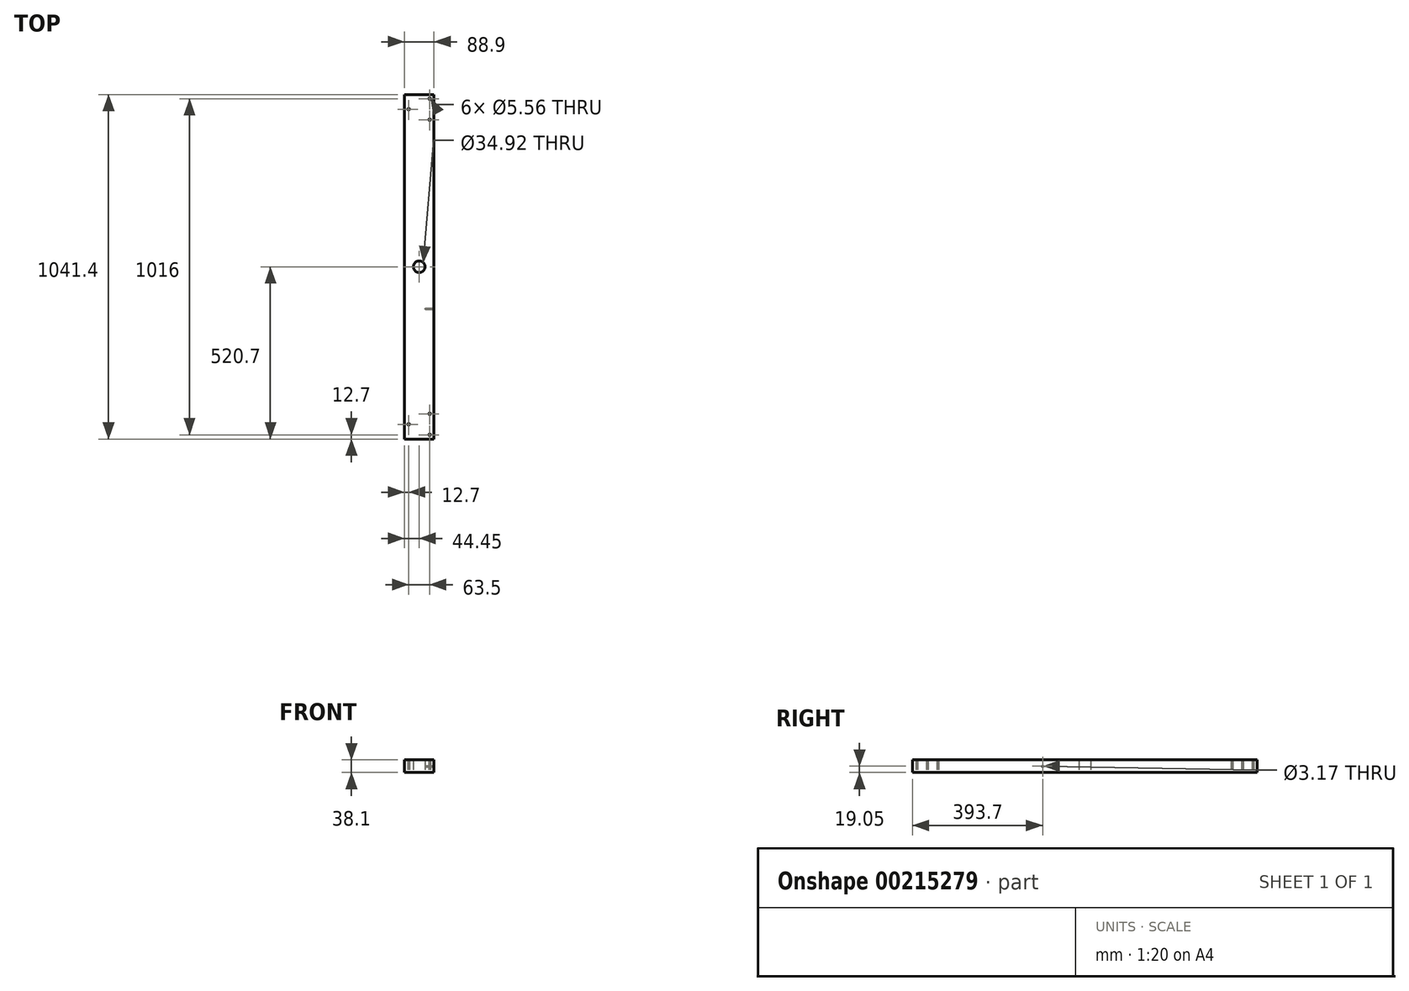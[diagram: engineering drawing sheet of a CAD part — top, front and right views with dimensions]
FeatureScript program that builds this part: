
annotation { "Feature Type Name" : "Feature", "Feature Type Description" : "" }
export const myFeature = defineFeature(function(context is Context, id is Id, definition is map)
    precondition{}
    {
        {
            var Q0;
            Q0=qCreatedBy(makeId("Top.planeOp"),FACE);
            var sketch = newSketch(context, id + "F0", { "sketchPlane" : qUnion([Q0])});
            skLineSegment(sketch, "E0.bottom", {"start": v(-44.45, 520.7) * mm, "end": v(44.45, 520.7) * mm});
            skLineSegment(sketch, "E0.top", {"start": v(-44.45, -520.7) * mm, "end": v(44.45, -520.7) * mm});
            skLineSegment(sketch, "E0.left", {"start": v(-44.45, 520.7) * mm, "end": v(-44.45, -520.7) * mm});
            skLineSegment(sketch, "E0.right", {"start": v(44.45, 520.7) * mm, "end": v(44.45, -520.7) * mm});
            skCircle(sketch, "E1", {"center": v(0, 0) * mm, "radius": 17.46 * mm});
            skLineSegment(sketch, "E2", {"start": v(-44.45, -431.8) * mm, "end": v(44.45, -431.8) * mm, "construction": true});
            skCircle(sketch, "E3", {"center": v(31.75, -444.5) * mm, "radius": 2.78 * mm});
            skCircle(sketch, "E4", {"center": v(-31.75, -476.25) * mm, "radius": 2.78 * mm});
            skCircle(sketch, "E5.MirrorC", {"center": v(31.75, 444.5) * mm, "radius": 2.78 * mm});
            skCircle(sketch, "E6.MirrorC", {"center": v(31.75, 508) * mm, "radius": 2.78 * mm});
            skCircle(sketch, "E7.MirrorC", {"center": v(-31.75, 476.25) * mm, "radius": 2.78 * mm});
            skLineSegment(sketch, "E8", {"start": v(-44.45, -476.25) * mm, "end": v(44.45, -476.25) * mm, "construction": true});
            skCircle(sketch, "E9.MirrorC", {"center": v(31.75, -508) * mm, "radius": 2.78 * mm});
            skSolve(sketch);
        }
        {
            var Q0;
            Q0=makeQuery(id+"F0.imprint","IMPRINT",FACE,{"disambiguationData":[TD([[makeQuery(id+"F0.imprint","IMPRINT",EDGE,{"derivedFrom":sQuery(id+"F0.wireOp",EDGE,"E0.bottom")}),-1.0]])]});
            extrude(context, id + "F1", {"entities" : qUnion([Q0]), "depth" : 38.1 * mm});
        }
        {
            var Q0;
            Q0=makeQuery(id+"F1.opExtrude","SWEPT_FACE",FACE,{"disambiguationData":[OSD([sQuery(id+"F0.wireOp",EDGE,"E0.right")])]});
            var sketch = newSketch(context, id + "F2", { "sketchPlane" : qUnion([Q0])});
            skPoint(sketch, "E10", {"position": v(-127, 19.05) * mm});
            skSolve(sketch);
        }
        {
            var Q0;
            Q0=sQuery(id+"F2.wireOp",VERTEX,"E10");
            var Q1;
            Q1=makeQuery(id+"F1.opExtrude","SWEPT_BODY",BODY,{"disambiguationData":[OSD([sQuery(id+"F0.wireOp",EDGE,"E0.bottom"),sQuery(id+"F0.wireOp",EDGE,"E0.top"),sQuery(id+"F0.wireOp",EDGE,"E0.left"),sQuery(id+"F0.wireOp",EDGE,"E0.right"),sQuery(id+"F0.wireOp",EDGE,"E1"),sQuery(id+"F0.wireOp",EDGE,"E3"),sQuery(id+"F0.wireOp",EDGE,"E4"),sQuery(id+"F0.wireOp",EDGE,"E5.MirrorC"),sQuery(id+"F0.wireOp",EDGE,"E6.MirrorC"),sQuery(id+"F0.wireOp",EDGE,"E7.MirrorC"),sQuery(id+"F0.wireOp",EDGE,"E9.MirrorC")])]});
            hole(context, id + "F3", {"style" : HoleStyle.SIMPLE, "endStyle" : HoleEndStyle.BLIND, "holeDiameter" : 3.17 * mm, "holeDepth" : 25.4 * mm, "startFromSketch" : true, "locations" : qUnion([Q0]), "scope" : qUnion([Q1])});
        }
    });
